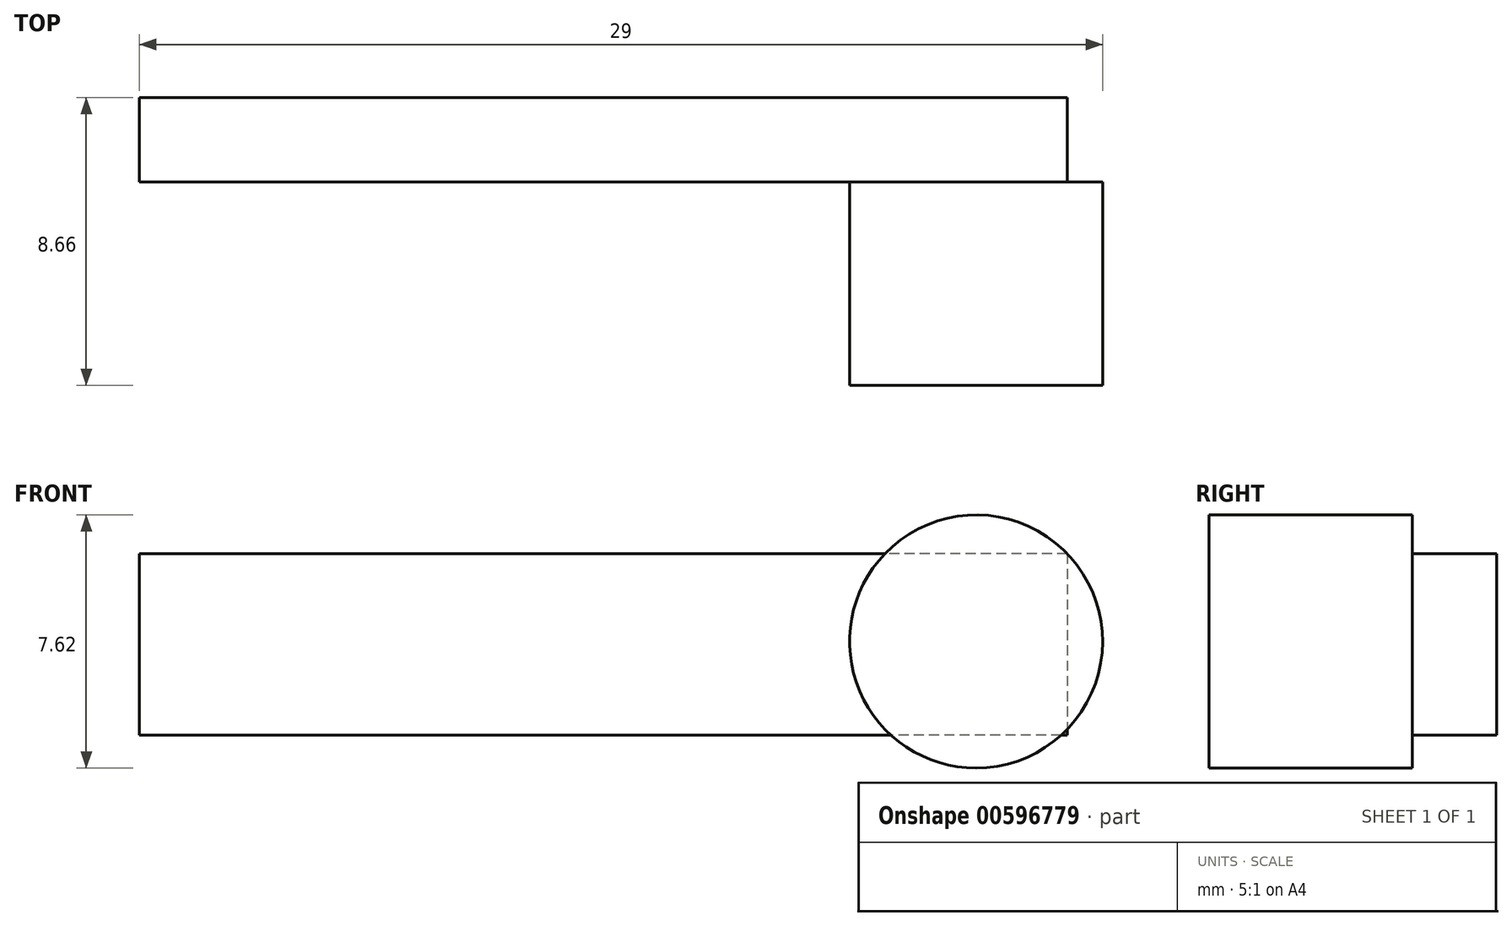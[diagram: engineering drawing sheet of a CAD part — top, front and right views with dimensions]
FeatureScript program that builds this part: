
annotation { "Feature Type Name" : "Feature", "Feature Type Description" : "" }
export const myFeature = defineFeature(function(context is Context, id is Id, definition is map)
    precondition{}
    {
        {
            var Q0;
            Q0=qCreatedBy(makeId("Front.planeOp"),FACE);
            var sketch = newSketch(context, id + "F0", { "sketchPlane" : qUnion([Q0])});
            skCircle(sketch, "E0", {"center": v(0, 0) * mm, "radius": 3.81 * mm});
            skSolve(sketch);
        }
        {
            var Q0;
            Q0=makeQuery(id+"F0.imprint","IMPRINT",FACE,{"disambiguationData":[TD([[makeQuery(id+"F0.imprint","IMPRINT",EDGE,{"derivedFrom":sQuery(id+"F0.wireOp",EDGE,"E0")}),1.0]])]});
            extrude(context, id + "F1", {"entities" : qUnion([Q0]), "depth" : 6.12 * mm, "offsetDistance" : 25.4 * mm});
        }
        {
            var Q0;
            Q0=makeQuery(id+"F1.opExtrude","CAP_FACE",FACE,{"disambiguationData":[OSD([sQuery(id+"F0.wireOp",EDGE,"E0")])],"isStart":true});
            var sketch = newSketch(context, id + "F2", { "sketchPlane" : qUnion([Q0])});
            skLineSegment(sketch, "E1.bottom", {"start": v(-2.75, 2.64) * mm, "end": v(25.2, 2.64) * mm});
            skLineSegment(sketch, "E1.top", {"start": v(-2.75, -2.82) * mm, "end": v(25.2, -2.82) * mm});
            skLineSegment(sketch, "E1.left", {"start": v(-2.75, 2.64) * mm, "end": v(-2.75, -2.82) * mm});
            skLineSegment(sketch, "E1.right", {"start": v(25.2, 2.64) * mm, "end": v(25.2, -2.82) * mm});
            skSolve(sketch);
        }
        {
            var Q0;
            Q0 = qSketchRegion(id + "F2", true);
            extrude(context, id + "F3", {"entities" : qUnion([Q0]), "operationType" : NewBodyOperationType.ADD, "depth" : 2.54 * mm, "offsetDistance" : 25.4 * mm});
        }
    });
